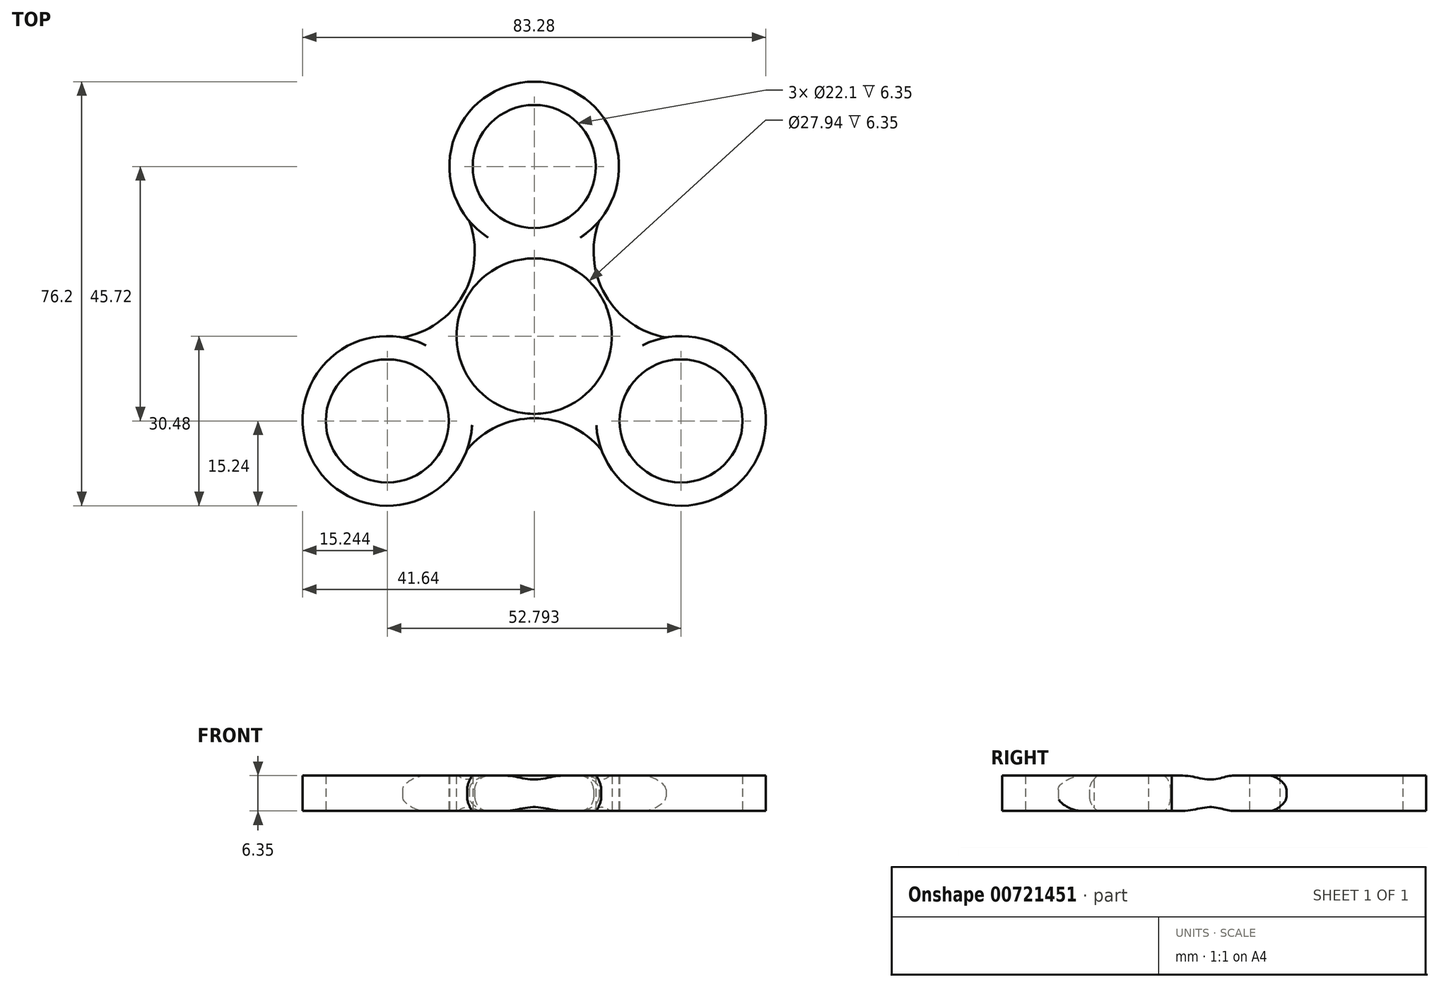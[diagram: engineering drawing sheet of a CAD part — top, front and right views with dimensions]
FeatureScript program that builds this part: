
annotation { "Feature Type Name" : "Feature", "Feature Type Description" : "" }
export const myFeature = defineFeature(function(context is Context, id is Id, definition is map)
    precondition{}
    {
        {
            var Q0;
            Q0=qCreatedBy(makeId("Top.planeOp"),FACE);
            var sketch = newSketch(context, id + "F0", { "sketchPlane" : qUnion([Q0])});
            skCircle(sketch, "E0", {"center": v(0, 0) * mm, "radius": 11.05 * mm});
            skCircle(sketch, "E1", {"center": v(0, 0) * mm, "radius": 13.97 * mm});
            skLineSegment(sketch, "E2", {"start": v(0, 0) * mm, "end": v(0, 30.48) * mm});
            skLineSegment(sketch, "E3", {"start": v(0, 30.48) * mm, "end": v(-11.63, 30.48) * mm});
            skCircle(sketch, "E4", {"center": v(0, 30.48) * mm, "radius": 11.05 * mm});
            skCircle(sketch, "E5", {"center": v(0, 30.48) * mm, "radius": 15.24 * mm});
            skCircle(sketch, "E6.1.0", {"center": v(-26.4, -15.24) * mm, "radius": 15.24 * mm});
            skCircle(sketch, "E6.2.0", {"center": v(26.4, -15.24) * mm, "radius": 15.24 * mm});
            skCircle(sketch, "E7.1.0", {"center": v(-26.4, -15.24) * mm, "radius": 11.05 * mm});
            skCircle(sketch, "E7.2.0", {"center": v(26.4, -15.24) * mm, "radius": 11.05 * mm});
            skLineSegment(sketch, "E8", {"start": v(0, 0) * mm, "end": v(-26.4, 15.24) * mm});
            skArc(sketch, "E9", {"start": v(-29.1, -0.24) * mm, "mid": v(-12.78, 7.38) * mm, "end": v(-14.34, 25.33) * mm});
            skArc(sketch, "E10.1.0", {"start": v(14.76, -25.09) * mm, "mid": v(0, -14.76) * mm, "end": v(-14.76, -25.09) * mm});
            skArc(sketch, "E10.2.0", {"start": v(14.34, 25.33) * mm, "mid": v(12.78, 7.38) * mm, "end": v(29.1, -0.24) * mm});
            skSolve(sketch);
        }
        {
            var Q0;
            Q0 = qSketchRegion(id + "F0", true);
            extrude(context, id + "F1", {"entities" : qUnion([Q0]), "depth" : 6.35 * mm, "offsetDistance" : 25.4 * mm});
        }
        {
            var Q0;
            Q0=makeQuery(id+"F1.opExtrude","CAP_EDGE",EDGE,{"disambiguationData":[OSD([sQuery(id+"F0.wireOp",EDGE,"E10.1.0")])],"isStart":false});
            fillet(context, id + "F2", {"entities" : qUnion([Q0]), "radius" : 2.54 * mm, "tangentPropagation" : true, "allowEdgeOverflow" : false});
        }
        {
            var Q0;
            Q0=makeQuery(id+"F1.opExtrude","CAP_EDGE",EDGE,{"disambiguationData":[OSD([sQuery(id+"F0.wireOp",EDGE,"E10.1.0")])],"isStart":true});
            fillet(context, id + "F3", {"entities" : qUnion([Q0]), "radius" : 2.54 * mm, "tangentPropagation" : true, "allowEdgeOverflow" : false});
        }
        {
            var Q0;
            Q0=makeQuery(id+"F1.opExtrude","CAP_EDGE",EDGE,{"disambiguationData":[OSD([sQuery(id+"F0.wireOp",EDGE,"E10.2.0")])],"isStart":false});
            var Q1;
            Q1=makeQuery(id+"F1.opExtrude","CAP_EDGE",EDGE,{"disambiguationData":[OSD([sQuery(id+"F0.wireOp",EDGE,"E10.2.0")])],"isStart":true});
            fillet(context, id + "F4", {"entities" : qUnion([Q0, Q1]), "radius" : 2.54 * mm, "tangentPropagation" : true, "allowEdgeOverflow" : false});
        }
        {
            var Q0;
            Q0=makeQuery(id+"F1.opExtrude","CAP_EDGE",EDGE,{"disambiguationData":[OSD([sQuery(id+"F0.wireOp",EDGE,"E9")])],"isStart":true});
            fillet(context, id + "F5", {"entities" : qUnion([Q0]), "radius" : 2.54 * mm, "tangentPropagation" : true, "allowEdgeOverflow" : false});
        }
        {
            var Q0;
            Q0=makeQuery(id+"F1.opExtrude","CAP_EDGE",EDGE,{"disambiguationData":[OSD([sQuery(id+"F0.wireOp",EDGE,"E9")])],"isStart":false});
            fillet(context, id + "F6", {"entities" : qUnion([Q0]), "radius" : 2.54 * mm, "tangentPropagation" : true, "allowEdgeOverflow" : false});
        }
    });
